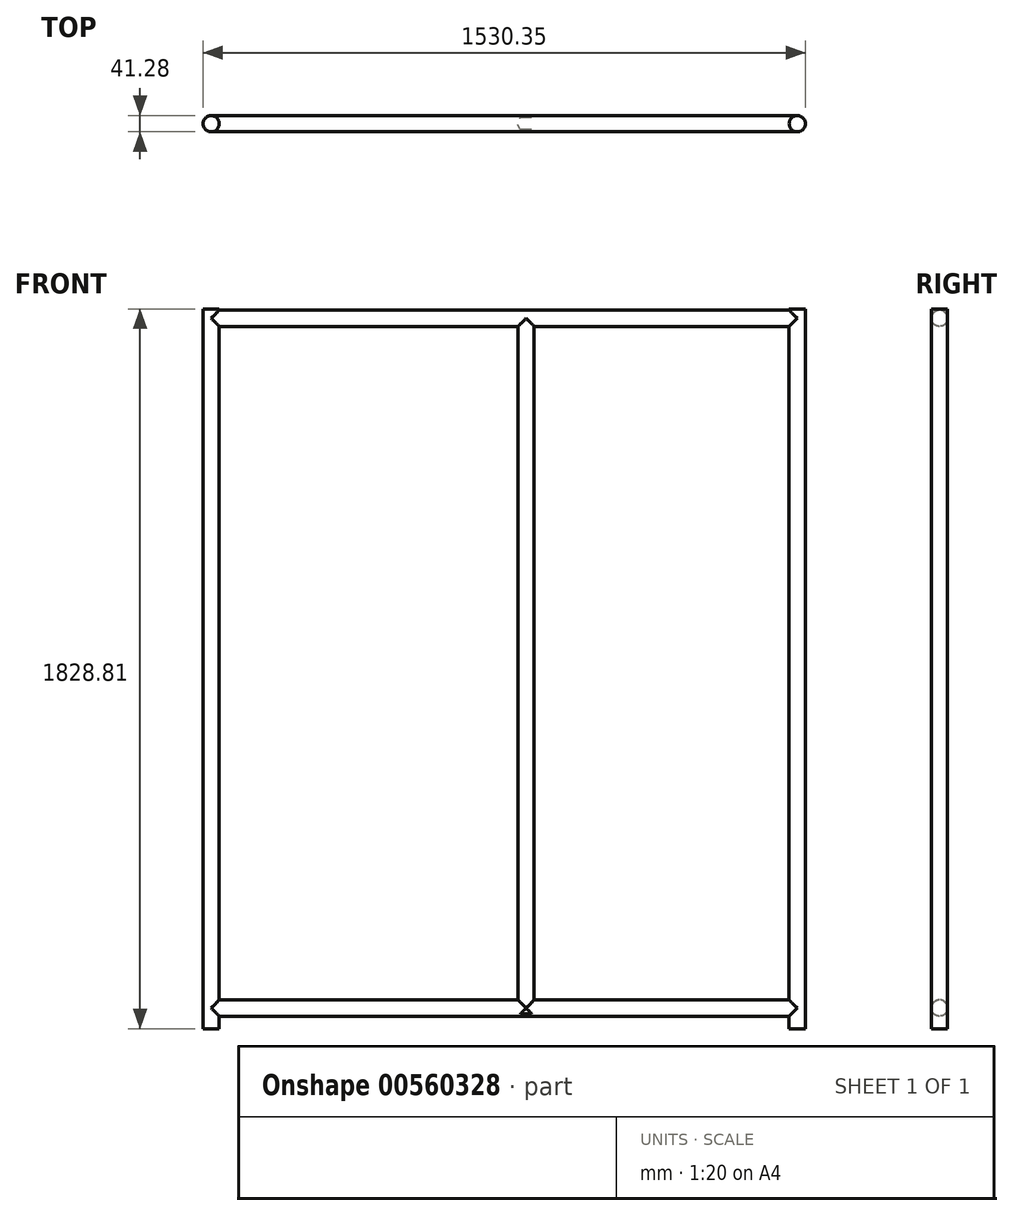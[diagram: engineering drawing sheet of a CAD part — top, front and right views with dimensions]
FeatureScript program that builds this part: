
annotation { "Feature Type Name" : "Feature", "Feature Type Description" : "" }
export const myFeature = defineFeature(function(context is Context, id is Id, definition is map)
    precondition{}
    {
        {
            var Q0;
            Q0=qCreatedBy(makeId("Top.planeOp"),FACE);
            var sketch = newSketch(context, id + "F0", { "sketchPlane" : qUnion([Q0])});
            skCircle(sketch, "E0", {"center": v(0, 0) * mm, "radius": 20.64 * mm});
            skCircle(sketch, "E1", {"center": v(1489.08, 0) * mm, "radius": 20.64 * mm});
            skLineSegment(sketch, "E2", {"start": v(0, 0) * mm, "end": v(1489.08, 0) * mm, "construction": true});
            skSolve(sketch);
        }
        {
            var Q0;
            Q0=makeQuery(id+"F0.imprint","IMPRINT",FACE,{"disambiguationData":[TD([[makeQuery(id+"F0.imprint","IMPRINT",EDGE,{"derivedFrom":sQuery(id+"F0.wireOp",EDGE,"E0")}),1.0]])]});
            var Q1;
            Q1=makeQuery(id+"F0.imprint","IMPRINT",FACE,{"disambiguationData":[TD([[makeQuery(id+"F0.imprint","IMPRINT",EDGE,{"derivedFrom":sQuery(id+"F0.wireOp",EDGE,"E1")}),1.0]])]});
            extrude(context, id + "F1", {"entities" : qUnion([Q0, Q1]), "depth" : 1828.8 * mm + 1 / 101.6 * mm, "offsetDistance" : 25.4 * mm});
        }
        {
            var Q0;
            Q0=qCreatedBy(makeId("Right.planeOp"),FACE);
            var sketch = newSketch(context, id + "F2", { "sketchPlane" : qUnion([Q0])});
            skCircle(sketch, "E3", {"center": v(0, 52.39) * mm, "radius": 20.64 * mm});
            skLineSegment(sketch, "E4", {"start": v(0, 0) * mm, "end": v(0, 2132.66) * mm, "construction": true});
            skCircle(sketch, "E5", {"center": v(0, 1804.99) * mm, "radius": 20.64 * mm});
            skLineSegment(sketch, "E6", {"start": v(72.47, 52.39) * mm, "end": v(-103.35, 52.39) * mm, "construction": true});
            skSolve(sketch);
        }
        {
            var Q0;
            Q0=makeQuery(id+"F2.imprint","IMPRINT",FACE,{"disambiguationData":[TD([[makeQuery(id+"F2.imprint","IMPRINT",EDGE,{"derivedFrom":sQuery(id+"F2.wireOp",EDGE,"E3")}),1.0]])]});
            var Q1;
            Q1=makeQuery(id+"F2.imprint","IMPRINT",FACE,{"disambiguationData":[TD([[makeQuery(id+"F2.imprint","IMPRINT",EDGE,{"derivedFrom":sQuery(id+"F2.wireOp",EDGE,"E5")}),1.0]])]});
            var Q2;
            Q2=makeQuery(id+"F1.opExtrude","SWEPT_BODY",BODY,{"disambiguationData":[OSD([sQuery(id+"F0.wireOp",EDGE,"E1")])]});
            extrude(context, id + "F3", {"entities" : qUnion([Q0, Q1]), "operationType" : NewBodyOperationType.ADD, "endBound" : BoundingType.UP_TO_BODY, "depth" : 184.9 * mm, "endBoundEntityBody" : qUnion([Q2]), "offsetDistance" : 25.4 * mm});
        }
        {
            var Q0;
            Q0=qCreatedBy(makeId("Top.planeOp"),FACE);
            cPlane(context, id + "F4", {"entities" : qUnion([Q0]), "cplaneType" : CPlaneType.OFFSET, "offset" : 25.4 * mm + 1 / 101.6 * mm + ((25.4 * mm + 5 / 203.2 * mm) / 2), "width" : 152.4 * mm, "height" : 152.4 * mm});
        }
        {
            var Q0;
            Q0=qCreatedBy(id+"F4.planeOp",FACE);
            var sketch = newSketch(context, id + "F5", { "sketchPlane" : qUnion([Q0])});
            skCircle(sketch, "E7", {"center": v(800.1, 0) * mm, "radius": 20.64 * mm});
            skLineSegment(sketch, "E8", {"start": v(0, 0) * mm, "end": v(1886.44, 0) * mm, "construction": true});
            skSolve(sketch);
        }
        {
            var Q0;
            Q0=makeQuery(id+"F5.imprint","IMPRINT",FACE,{"disambiguationData":[TD([[makeQuery(id+"F5.imprint","IMPRINT",EDGE,{"derivedFrom":sQuery(id+"F5.wireOp",EDGE,"E7")}),1.0]])]});
            var Q1;
            Q1=makeQuery(id+"F3.opExtrude","SWEPT_FACE",FACE,{"disambiguationData":[OSD([sQuery(id+"F2.wireOp",EDGE,"E5")])]});
            extrude(context, id + "F6", {"entities" : qUnion([Q0]), "operationType" : NewBodyOperationType.ADD, "endBound" : BoundingType.UP_TO_SURFACE, "depth" : 25.4 * mm, "endBoundEntityFace" : qUnion([Q1]), "offsetDistance" : 25.4 * mm});
        }
    });
